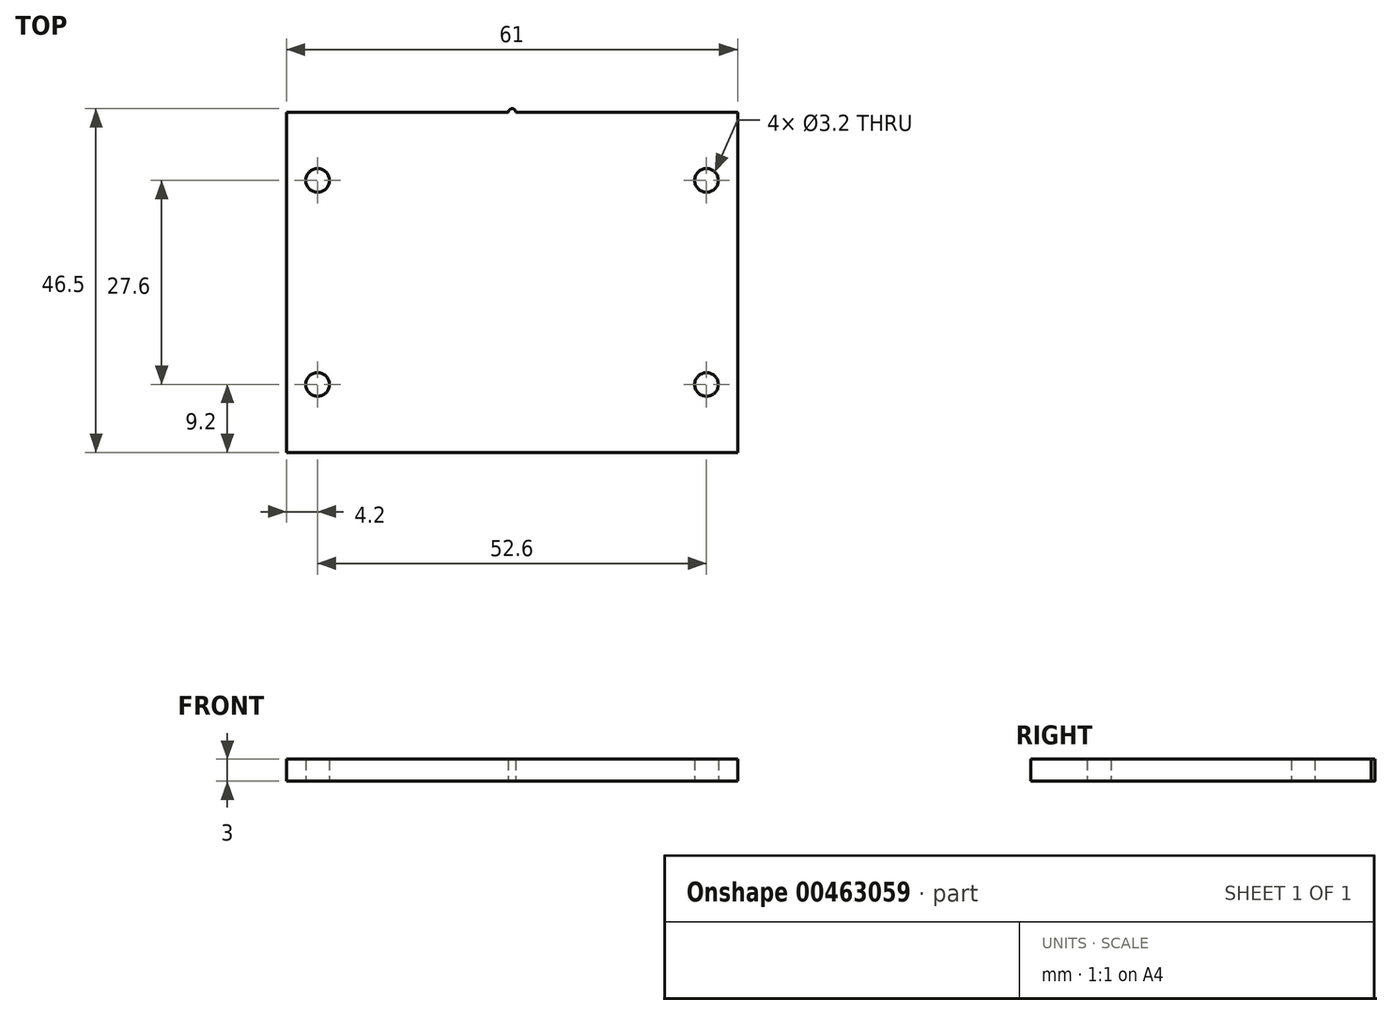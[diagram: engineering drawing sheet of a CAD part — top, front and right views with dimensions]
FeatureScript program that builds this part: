
annotation { "Feature Type Name" : "Feature", "Feature Type Description" : "" }
export const myFeature = defineFeature(function(context is Context, id is Id, definition is map)
    precondition{}
    {
        {
            var Q0;
            Q0=qCreatedBy(makeId("Top.planeOp"),FACE);
            var sketch = newSketch(context, id + "F0", { "sketchPlane" : qUnion([Q0])});
            skLineSegment(sketch, "E0.bottom", {"start": v(-30.5, 23) * mm, "end": v(30.5, 23) * mm});
            skLineSegment(sketch, "E0.top", {"start": v(-30.5, -23) * mm, "end": v(30.5, -23) * mm});
            skLineSegment(sketch, "E0.left", {"start": v(-30.5, 23) * mm, "end": v(-30.5, -23) * mm});
            skLineSegment(sketch, "E0.right", {"start": v(30.5, 23) * mm, "end": v(30.5, -23) * mm});
            skCircle(sketch, "E1", {"center": v(-26.3, 13.8) * mm, "radius": 1.6 * mm});
            skCircle(sketch, "E2", {"center": v(26.3, 13.8) * mm, "radius": 1.6 * mm});
            skCircle(sketch, "E3", {"center": v(26.3, -13.8) * mm, "radius": 1.6 * mm});
            skCircle(sketch, "E4", {"center": v(-26.3, -13.8) * mm, "radius": 1.6 * mm});
            skCircle(sketch, "E5", {"center": v(0, 23) * mm, "radius": 0.5 * mm});
            skPoint(sketch, "E6.endSnap0", {"position": v(30.5, 0) * mm});
            skSolve(sketch);
        }
        {
            var Q0;
            Q0=qSketchRegion(id+"F0",true);
            extrude(context, id + "F1", {"entities" : qUnion([Q0]), "depth" : 3 * mm});
        }
    });
